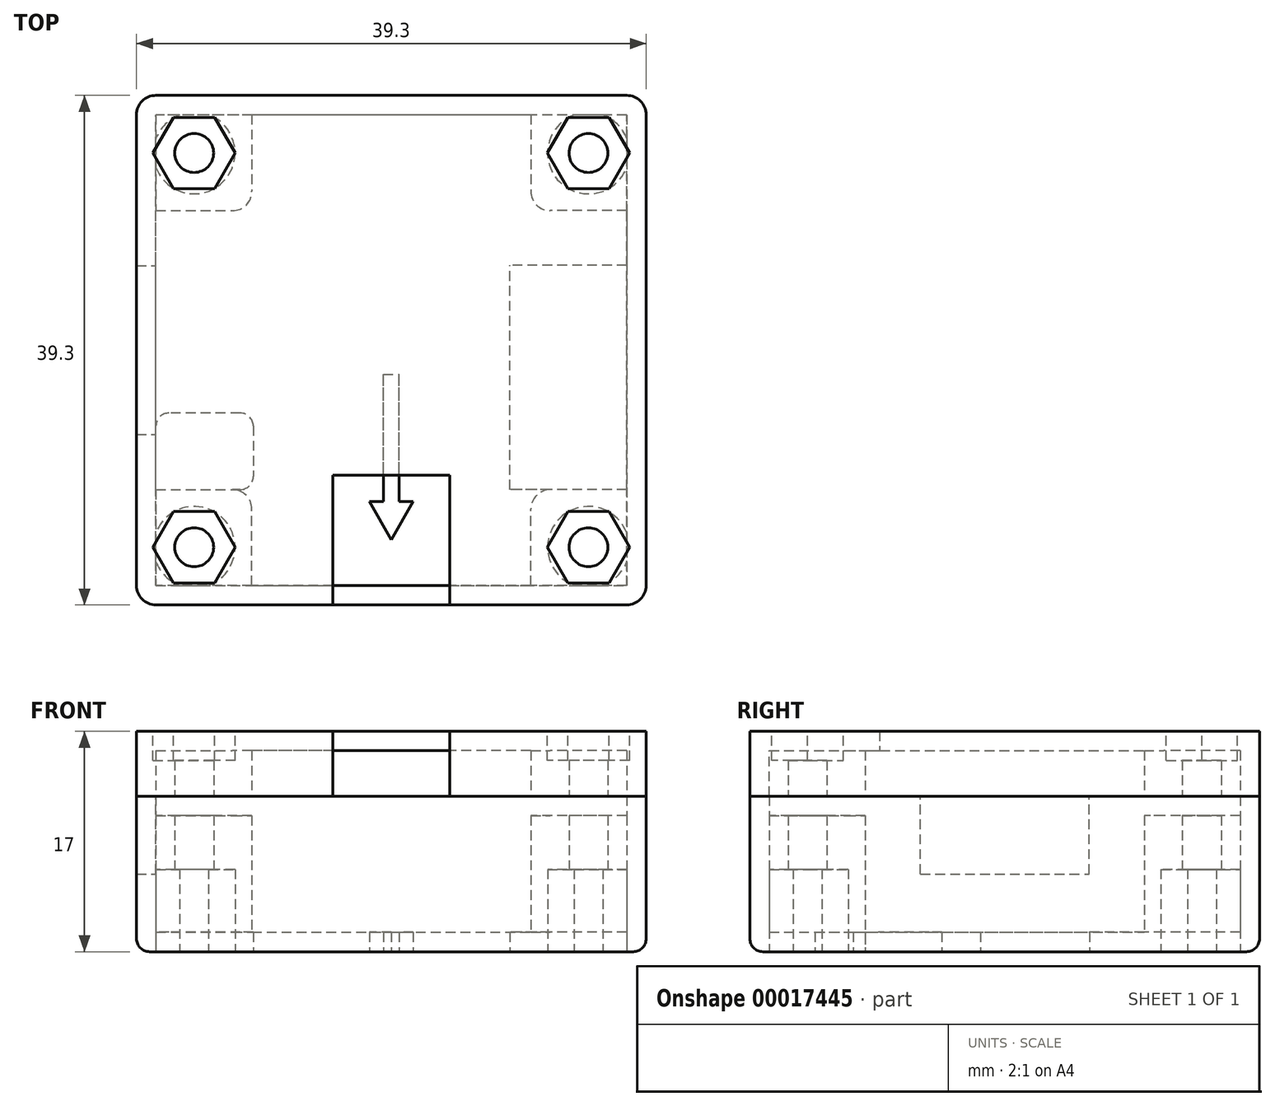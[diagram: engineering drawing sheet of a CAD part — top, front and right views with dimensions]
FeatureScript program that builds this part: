
annotation { "Feature Type Name" : "Feature", "Feature Type Description" : "" }
export const myFeature = defineFeature(function(context is Context, id is Id, definition is map)
    precondition{}
    {
        {
            var Q0;
            Q0=qCreatedBy(makeId("Top.planeOp"),FACE);
            var sketch = newSketch(context, id + "F0", { "sketchPlane" : qUnion([Q0])});
            skLineSegment(sketch, "E0.rect.bottom", {"start": v(18.15, -19.65) * mm, "end": v(-18.15, -19.65) * mm});
            skLineSegment(sketch, "E0.rect.top", {"start": v(18.15, 19.65) * mm, "end": v(-18.15, 19.65) * mm});
            skLineSegment(sketch, "E0.rect.left", {"start": v(19.65, -18.15) * mm, "end": v(19.65, 18.15) * mm});
            skLineSegment(sketch, "E0.rect.right", {"start": v(-19.65, -18.15) * mm, "end": v(-19.65, 18.15) * mm});
            skPoint(sketch, "E0.rect.middle", {"position": v(0, 0) * mm});
            skCircle(sketch, "E1", {"center": v(0, 0) * mm, "radius": 21.5 * mm, "construction": true});
            skLineSegment(sketch, "E2", {"start": v(0, 0) * mm, "end": v(19.65, 19.65) * mm, "construction": true});
            skCircle(sketch, "E3", {"center": v(15.2, 15.2) * mm, "radius": 1.5 * mm});
            skArc(sketch, "E4", {"start": v(14.1, 18.15) * mm, "mid": v(12.98, 12.98) * mm, "end": v(18.15, 14.1) * mm});
            skPoint(sketch, "E5.visualSharp", {"position": v(19.65, 19.65) * mm});
            skArc(sketch, "E5.filletArc", {"start": v(19.65, 18.15) * mm, "mid": v(19.21, 19.21) * mm, "end": v(18.15, 19.65) * mm});
            skLineSegment(sketch, "E6.rect.bottom", {"start": v(18.15, 19.65) * mm, "end": v(10.76, 19.65) * mm});
            skLineSegment(sketch, "E6.rect.top", {"start": v(18.15, 10.76) * mm, "end": v(12.26, 10.76) * mm});
            skLineSegment(sketch, "E6.rect.left", {"start": v(19.65, 18.15) * mm, "end": v(19.65, 10.76) * mm});
            skLineSegment(sketch, "E6.rect.right", {"start": v(10.76, 18.15) * mm, "end": v(10.76, 12.26) * mm});
            skPoint(sketch, "E7.visualSharp", {"position": v(10.76, 10.76) * mm});
            skArc(sketch, "E7.filletArc", {"start": v(10.76, 12.26) * mm, "mid": v(11.2, 11.2) * mm, "end": v(12.26, 10.76) * mm});
            skArc(sketch, "E8.1.1", {"start": v(-16.31, 18.15) * mm, "mid": v(-17.43, 17.43) * mm, "end": v(-18.15, 16.31) * mm});
            skCircle(sketch, "E8.1.2", {"center": v(-15.2, 15.2) * mm, "radius": 1.5 * mm});
            skLineSegment(sketch, "E8.1.3", {"start": v(-18.15, 10.76) * mm, "end": v(-12.26, 10.76) * mm});
            skArc(sketch, "E8.1.4", {"start": v(-12.26, 10.76) * mm, "mid": v(-11.2, 11.2) * mm, "end": v(-10.76, 12.26) * mm});
            skLineSegment(sketch, "E8.1.5", {"start": v(-10.76, 18.15) * mm, "end": v(-10.76, 12.26) * mm});
            skLineSegment(sketch, "E8.1.6", {"start": v(-18.15, 19.65) * mm, "end": v(-10.76, 19.65) * mm});
            skArc(sketch, "E8.1.7", {"start": v(-18.15, 19.65) * mm, "mid": v(-19.21, 19.21) * mm, "end": v(-19.65, 18.15) * mm});
            skLineSegment(sketch, "E8.1.8", {"start": v(-19.65, 18.15) * mm, "end": v(-19.65, 10.76) * mm});
            skArc(sketch, "E8.2.1", {"start": v(-18.15, -16.31) * mm, "mid": v(-17.43, -17.43) * mm, "end": v(-16.31, -18.15) * mm});
            skCircle(sketch, "E8.2.2", {"center": v(-15.2, -15.2) * mm, "radius": 1.5 * mm});
            skLineSegment(sketch, "E8.2.3", {"start": v(-10.76, -18.15) * mm, "end": v(-10.76, -12.26) * mm});
            skArc(sketch, "E8.2.4", {"start": v(-10.76, -12.26) * mm, "mid": v(-11.2, -11.2) * mm, "end": v(-12.26, -10.76) * mm});
            skLineSegment(sketch, "E8.2.5", {"start": v(-18.15, -10.76) * mm, "end": v(-12.26, -10.76) * mm});
            skLineSegment(sketch, "E8.2.6", {"start": v(-19.65, -18.15) * mm, "end": v(-19.65, -10.76) * mm});
            skArc(sketch, "E8.2.7", {"start": v(-19.65, -18.15) * mm, "mid": v(-19.21, -19.21) * mm, "end": v(-18.15, -19.65) * mm});
            skLineSegment(sketch, "E8.2.8", {"start": v(-18.15, -19.65) * mm, "end": v(-10.76, -19.65) * mm});
            skArc(sketch, "E9.2.3.0", {"start": v(18.15, -14.1) * mm, "mid": v(12.98, -12.98) * mm, "end": v(14.1, -18.15) * mm});
            skCircle(sketch, "E9.4.3.0", {"center": v(15.2, -15.2) * mm, "radius": 1.5 * mm});
            skArc(sketch, "E9.9.3.0", {"start": v(12.26, -10.76) * mm, "mid": v(11.2, -11.2) * mm, "end": v(10.76, -12.26) * mm});
            skLineSegment(sketch, "E9.16.3.0", {"start": v(18.15, -19.65) * mm, "end": v(10.76, -19.65) * mm});
            skArc(sketch, "E9.19.3.0", {"start": v(18.15, -19.65) * mm, "mid": v(19.21, -19.21) * mm, "end": v(19.65, -18.15) * mm});
            skLineSegment(sketch, "E9.23.3.0", {"start": v(19.65, -18.15) * mm, "end": v(19.65, -10.76) * mm});
            skPoint(sketch, "E10.orphan", {"position": v(-19.65, 19.65) * mm});
            skPoint(sketch, "E11.orphan", {"position": v(19.65, -19.65) * mm});
            skPoint(sketch, "E12.orphan", {"position": v(-19.65, -19.65) * mm});
            skLineSegment(sketch, "E13.trimOffspring", {"start": v(14.1, 18.15) * mm, "end": v(-14.1, 18.15) * mm});
            skLineSegment(sketch, "E14.trimOffspring", {"start": v(-18.15, -14.1) * mm, "end": v(-18.15, 14.1) * mm});
            skLineSegment(sketch, "E15.trimOffspring", {"start": v(14.1, -18.15) * mm, "end": v(-14.1, -18.15) * mm});
            skLineSegment(sketch, "E16.trimOffspring", {"start": v(18.15, -14.1) * mm, "end": v(18.15, 14.1) * mm});
            skLineSegment(sketch, "E17", {"start": v(-14.1, 18.15) * mm, "end": v(-18.15, 18.15) * mm});
            skLineSegment(sketch, "E18", {"start": v(-18.15, 18.15) * mm, "end": v(-18.15, 14.1) * mm});
            skLineSegment(sketch, "E19", {"start": v(14.1, 18.15) * mm, "end": v(18.15, 18.15) * mm});
            skLineSegment(sketch, "E20", {"start": v(18.15, 18.15) * mm, "end": v(18.15, 14.1) * mm});
            skLineSegment(sketch, "E21", {"start": v(18.15, -14.1) * mm, "end": v(18.15, -18.15) * mm});
            skLineSegment(sketch, "E22", {"start": v(14.1, -18.15) * mm, "end": v(18.15, -18.15) * mm});
            skLineSegment(sketch, "E23", {"start": v(-14.1, -18.15) * mm, "end": v(-18.15, -18.15) * mm});
            skLineSegment(sketch, "E24", {"start": v(-18.15, -14.1) * mm, "end": v(-18.15, -18.15) * mm});
            skLineSegment(sketch, "E25.trimOffspring", {"start": v(18.15, -10.76) * mm, "end": v(12.26, -10.76) * mm});
            skLineSegment(sketch, "E26.trimOffspring", {"start": v(10.76, -18.15) * mm, "end": v(10.76, -12.26) * mm});
            skArc(sketch, "E27.trimOffspring", {"start": v(-18.15, 14.1) * mm, "mid": v(-12.98, 12.98) * mm, "end": v(-14.1, 18.15) * mm});
            skArc(sketch, "E28.trimOffspring", {"start": v(18.15, 16.31) * mm, "mid": v(17.43, 17.43) * mm, "end": v(16.31, 18.15) * mm});
            skArc(sketch, "E29.trimOffspring", {"start": v(16.31, -18.15) * mm, "mid": v(17.43, -17.43) * mm, "end": v(18.15, -16.31) * mm});
            skArc(sketch, "E30.trimOffspring", {"start": v(-14.1, -18.15) * mm, "mid": v(-12.98, -12.98) * mm, "end": v(-18.15, -14.1) * mm});
            skLineSegment(sketch, "E31", {"start": v(-26.46, -4.85) * mm, "end": v(25.33, -4.85) * mm, "construction": true});
            skLineSegment(sketch, "E32", {"start": v(-10.65, -23.17) * mm, "end": v(-10.65, 21.13) * mm, "construction": true});
            skLineSegment(sketch, "E33.bottom", {"start": v(-11.65, -4.85) * mm, "end": v(-17.15, -4.85) * mm});
            skLineSegment(sketch, "E33.top", {"start": v(-11.65, -10.76) * mm, "end": v(-17.15, -10.76) * mm});
            skLineSegment(sketch, "E33.left", {"start": v(-10.65, -5.85) * mm, "end": v(-10.65, -9.76) * mm});
            skLineSegment(sketch, "E33.right", {"start": v(-18.15, -5.85) * mm, "end": v(-18.15, -9.76) * mm});
            skPoint(sketch, "E34.visualSharp", {"position": v(-10.65, -10.76) * mm});
            skArc(sketch, "E34.filletArc", {"start": v(-11.65, -10.76) * mm, "mid": v(-10.94, -10.46) * mm, "end": v(-10.65, -9.76) * mm});
            skPoint(sketch, "E35.visualSharp", {"position": v(-10.65, -4.85) * mm});
            skArc(sketch, "E35.filletArc", {"start": v(-10.65, -5.85) * mm, "mid": v(-10.94, -5.14) * mm, "end": v(-11.65, -4.85) * mm});
            skPoint(sketch, "E36.visualSharp", {"position": v(-18.15, -4.85) * mm});
            skArc(sketch, "E36.filletArc", {"start": v(-17.15, -4.85) * mm, "mid": v(-17.86, -5.14) * mm, "end": v(-18.15, -5.85) * mm});
            skPoint(sketch, "E37.visualSharp", {"position": v(-18.15, -10.76) * mm});
            skArc(sketch, "E37.filletArc", {"start": v(-18.15, -9.76) * mm, "mid": v(-17.86, -10.46) * mm, "end": v(-17.15, -10.76) * mm});
            skLineSegment(sketch, "E38", {"start": v(9.15, -24.31) * mm, "end": v(9.15, 23.94) * mm, "construction": true});
            skLineSegment(sketch, "E39", {"start": v(-23.3, 6.55) * mm, "end": v(24.8, 6.55) * mm, "construction": true});
            skLineSegment(sketch, "E40.bottom", {"start": v(18.15, -10.76) * mm, "end": v(9.15, -10.76) * mm});
            skLineSegment(sketch, "E40.top", {"start": v(18.15, 6.55) * mm, "end": v(9.15, 6.55) * mm});
            skLineSegment(sketch, "E40.left", {"start": v(18.15, -10.76) * mm, "end": v(18.15, 6.55) * mm});
            skLineSegment(sketch, "E40.right", {"start": v(9.15, -10.76) * mm, "end": v(9.15, 6.55) * mm});
            skLineSegment(sketch, "E41", {"start": v(0, -14.62) * mm, "end": v(1.68, -11.69) * mm});
            skLineSegment(sketch, "E42", {"start": v(1.68, -11.69) * mm, "end": v(0.61, -11.69) * mm});
            skLineSegment(sketch, "E43", {"start": v(0.61, -11.69) * mm, "end": v(0.61, -1.87) * mm});
            skLineSegment(sketch, "E44", {"start": v(0.61, -1.87) * mm, "end": v(0, -1.87) * mm});
            skLineSegment(sketch, "E45.MirrorCS", {"start": v(0, -14.62) * mm, "end": v(-1.68, -11.69) * mm});
            skLineSegment(sketch, "E46.MirrorCS", {"start": v(-1.68, -11.69) * mm, "end": v(-0.61, -11.69) * mm});
            skLineSegment(sketch, "E47.MirrorCS", {"start": v(-0.61, -11.69) * mm, "end": v(-0.61, -1.87) * mm});
            skLineSegment(sketch, "E48.MirrorCS", {"start": v(-0.61, -1.87) * mm, "end": v(0, -1.87) * mm});
            skSolve(sketch);
        }
        {
            var Q0;
            Q0=makeQuery(id+"F0.imprint","IMPRINT",FACE,{"disambiguationData":[TD([[makeQuery(id+"F0.imprint","IMPRINT",EDGE,{"derivedFrom":sQuery(id+"F0.wireOp",EDGE,"E0.rect.bottom")}),-1.0]])]});
            extrude(context, id + "F1", {"entities" : qUnion([Q0]), "depth" : 12 * mm});
        }
        {
            var Q0;
            {var subQ2=sQuery(id+"F0.wireOp",EDGE,"E8.1.3");Q0=makeQuery(id+"F0.imprint","IMPRINT",FACE,{"disambiguationData":[TD([[makeQuery(id+"F0.imprint","IMPRINT",EDGE,{"derivedFrom":subQ2}),1.0]])]});}
            var Q1;
            {var subQ3=sQuery(id+"F0.wireOp",EDGE,"E8.1.1");Q1=makeQuery(id+"F0.imprint","IMPRINT",FACE,{"disambiguationData":[TD([[makeQuery(id+"F0.imprint","IMPRINT",EDGE,{"derivedFrom":subQ3}),-1.0]])]});}
            var Q2;
            {var subQ2=sQuery(id+"F0.wireOp",EDGE,"E4");Q2=makeQuery(id+"F0.imprint","IMPRINT",FACE,{"disambiguationData":[TD([[makeQuery(id+"F0.imprint","IMPRINT",EDGE,{"derivedFrom":subQ2}),-1.0]])]});}
            var Q3;
            {var subQ0=sQuery(id+"F0.wireOp",EDGE,"E28.trimOffspring");Q3=makeQuery(id+"F0.imprint","IMPRINT",FACE,{"disambiguationData":[TD([[makeQuery(id+"F0.imprint","IMPRINT",EDGE,{"derivedFrom":subQ0}),-1.0]])]});}
            var Q4;
            {var subQ2=sQuery(id+"F0.wireOp",EDGE,"E8.2.3");Q4=makeQuery(id+"F0.imprint","IMPRINT",FACE,{"disambiguationData":[TD([[makeQuery(id+"F0.imprint","IMPRINT",EDGE,{"derivedFrom":subQ2}),1.0]])]});}
            var Q5;
            {var subQ3=sQuery(id+"F0.wireOp",EDGE,"E8.2.1");Q5=makeQuery(id+"F0.imprint","IMPRINT",FACE,{"disambiguationData":[TD([[makeQuery(id+"F0.imprint","IMPRINT",EDGE,{"derivedFrom":subQ3}),-1.0]])]});}
            var Q6;
            {var subQ3=sQuery(id+"F0.wireOp",EDGE,"E9.2.3.0");Q6=makeQuery(id+"F0.imprint","IMPRINT",FACE,{"disambiguationData":[TD([[makeQuery(id+"F0.imprint","IMPRINT",EDGE,{"derivedFrom":subQ3}),-1.0]])]});}
            var Q7;
            {var subQ0=sQuery(id+"F0.wireOp",EDGE,"E29.trimOffspring");Q7=makeQuery(id+"F0.imprint","IMPRINT",FACE,{"disambiguationData":[TD([[makeQuery(id+"F0.imprint","IMPRINT",EDGE,{"derivedFrom":subQ0}),-1.0]])]});}
            extrude(context, id + "F2", {"entities" : qUnion([Q0, Q1, Q2, Q3, Q4, Q5, Q6, Q7]), "operationType" : NewBodyOperationType.ADD, "depth" : 10.5 * mm});
        }
        {
            var Q0;
            {var subQ2=sQuery(id+"F0.wireOp",EDGE,"E8.1.1");Q0=makeQuery(id+"F0.imprint","IMPRINT",FACE,{"disambiguationData":[TD([[makeQuery(id+"F0.imprint","IMPRINT",EDGE,{"derivedFrom":subQ2}),1.0]])]});}
            var Q1;
            Q1=makeQuery(id+"F0.imprint","IMPRINT",FACE,{"disambiguationData":[TD([[makeQuery(id+"F0.imprint","IMPRINT",EDGE,{"derivedFrom":sQuery(id+"F0.wireOp",EDGE,"E3")}),-1.0]])]});
            var Q2;
            {var subQ2=sQuery(id+"F0.wireOp",EDGE,"E9.2.3.0");Q2=makeQuery(id+"F0.imprint","IMPRINT",FACE,{"disambiguationData":[TD([[makeQuery(id+"F0.imprint","IMPRINT",EDGE,{"derivedFrom":subQ2}),1.0]])]});}
            var Q3;
            {var subQ2=sQuery(id+"F0.wireOp",EDGE,"E8.2.1");Q3=makeQuery(id+"F0.imprint","IMPRINT",FACE,{"disambiguationData":[TD([[makeQuery(id+"F0.imprint","IMPRINT",EDGE,{"derivedFrom":subQ2}),1.0]])]});}
            extrude(context, id + "F3", {"entities" : qUnion([Q0, Q1, Q2, Q3]), "operationType" : NewBodyOperationType.ADD, "depth" : 10.5 * mm, "hasSecondDirection" : true, "secondDirectionOppositeDirection" : false, "secondDirectionDepth" : 6.35 * mm});
        }
        {
            var Q0;
            Q0 = qSketchRegion(id + "F0", true);
            var Q1;
            {var subQ2=sQuery(id+"F0.wireOp",EDGE,"E6.rect.top");Q1=makeQuery(id+"F0.imprint","IMPRINT",FACE,{"disambiguationData":[TD([[makeQuery(id+"F0.imprint","IMPRINT",EDGE,{"derivedFrom":subQ2}),1.0]])]});}
            extrude(context, id + "F4", {"entities" : qUnion([Q0, Q1]), "operationType" : NewBodyOperationType.ADD, "depth" : 1.5 * mm});
        }
        {
            var Q0;
            Q0=makeQuery(id+"F0.imprint","IMPRINT",FACE,{"disambiguationData":[TD([[makeQuery(id+"F0.imprint","IMPRINT",EDGE,{"derivedFrom":sQuery(id+"F0.wireOp",EDGE,"E33.bottom")}),1.0]])]});
            extrude(context, id + "F5", {"entities" : qUnion([Q0]), "operationType" : NewBodyOperationType.REMOVE, "depth" : 1.5 * mm});
        }
        {
            var Q0;
            Q0=makeQuery(id+"F0.imprint","IMPRINT",FACE,{"disambiguationData":[TD([[makeQuery(id+"F0.imprint","IMPRINT",EDGE,{"derivedFrom":sQuery(id+"F0.wireOp",EDGE,"E40.top")}),1.0]])]});
            extrude(context, id + "F6", {"entities" : qUnion([Q0]), "operationType" : NewBodyOperationType.REMOVE, "depth" : 1.5 * mm});
        }
        {
            var Q0;
            Q0=makeQuery(id+"F0.imprint","IMPRINT",FACE,{"disambiguationData":[TD([[makeQuery(id+"F0.imprint","IMPRINT",EDGE,{"derivedFrom":sQuery(id+"F0.wireOp",EDGE,"E41")}),1.0]])]});
            extrude(context, id + "F7", {"entities" : qUnion([Q0]), "operationType" : NewBodyOperationType.REMOVE, "depth" : 1.5 * mm});
        }
        {
            var Q0;
            Q0=makeQuery(id+"F1.opExtrude","CAP_FACE",FACE,{"disambiguationData":[OSD([sQuery(id+"F0.wireOp",EDGE,"E0.rect.bottom"),sQuery(id+"F0.wireOp",EDGE,"E0.rect.top"),sQuery(id+"F0.wireOp",EDGE,"E0.rect.left"),sQuery(id+"F0.wireOp",EDGE,"E0.rect.right"),sQuery(id+"F0.wireOp",EDGE,"E5.filletArc"),sQuery(id+"F0.wireOp",EDGE,"E6.rect.bottom"),sQuery(id+"F0.wireOp",EDGE,"E6.rect.left"),sQuery(id+"F0.wireOp",EDGE,"E8.1.6"),sQuery(id+"F0.wireOp",EDGE,"E8.1.7"),sQuery(id+"F0.wireOp",EDGE,"E8.1.8"),sQuery(id+"F0.wireOp",EDGE,"E8.2.6"),sQuery(id+"F0.wireOp",EDGE,"E8.2.7"),sQuery(id+"F0.wireOp",EDGE,"E8.2.8"),sQuery(id+"F0.wireOp",EDGE,"E9.16.3.0"),sQuery(id+"F0.wireOp",EDGE,"E9.19.3.0"),sQuery(id+"F0.wireOp",EDGE,"E9.23.3.0"),sQuery(id+"F0.wireOp",EDGE,"E13.trimOffspring"),sQuery(id+"F0.wireOp",EDGE,"E14.trimOffspring"),sQuery(id+"F0.wireOp",EDGE,"E15.trimOffspring"),sQuery(id+"F0.wireOp",EDGE,"E16.trimOffspring"),sQuery(id+"F0.wireOp",EDGE,"E17"),sQuery(id+"F0.wireOp",EDGE,"E18"),sQuery(id+"F0.wireOp",EDGE,"E19"),sQuery(id+"F0.wireOp",EDGE,"E20"),sQuery(id+"F0.wireOp",EDGE,"E21"),sQuery(id+"F0.wireOp",EDGE,"E22"),sQuery(id+"F0.wireOp",EDGE,"E23"),sQuery(id+"F0.wireOp",EDGE,"E24"),sQuery(id+"F0.wireOp",EDGE,"E33.right"),sQuery(id+"F0.wireOp",EDGE,"E40.left")])],"isStart":false});
            var sketch = newSketch(context, id + "F8", { "sketchPlane" : qUnion([Q0])});
            skLineSegment(sketch, "E49.bottom", {"start": v(-19.65, 6.5) * mm, "end": v(-18.15, 6.5) * mm});
            skLineSegment(sketch, "E49.top", {"start": v(-19.65, -6.5) * mm, "end": v(-18.15, -6.5) * mm});
            skLineSegment(sketch, "E49.left", {"start": v(-19.65, 6.5) * mm, "end": v(-19.65, -6.5) * mm});
            skLineSegment(sketch, "E49.right", {"start": v(-18.15, 6.5) * mm, "end": v(-18.15, -6.5) * mm});
            skLineSegment(sketch, "E50", {"start": v(-25.19, 6.5) * mm, "end": v(-14.9, 6.5) * mm, "construction": true});
            skSolve(sketch);
        }
        {
            var Q0;
            Q0 = qSketchRegion(id + "F8", true);
            extrude(context, id + "F9", {"entities" : qUnion([Q0]), "operationType" : NewBodyOperationType.REMOVE, "oppositeDirection" : true, "depth" : 6 * mm});
        }
        {
            var Q0;
            Q0=makeQuery(id+"F1.opExtrude","CAP_EDGE",EDGE,{"disambiguationData":[OSD([sQuery(id+"F0.wireOp",EDGE,"E0.rect.left"),sQuery(id+"F0.wireOp",EDGE,"E6.rect.left"),sQuery(id+"F0.wireOp",EDGE,"E9.23.3.0")])],"isStart":true});
            fillet(context, id + "F10", {"entities" : qUnion([Q0]), "radius" : 1 * mm, "tangentPropagation" : true, "allowEdgeOverflow" : false});
        }
        {
            var Q0;
            Q0=makeQuery(id+"F1.opExtrude","CAP_FACE",FACE,{"disambiguationData":[OSD([sQuery(id+"F0.wireOp",EDGE,"E0.rect.bottom"),sQuery(id+"F0.wireOp",EDGE,"E0.rect.top"),sQuery(id+"F0.wireOp",EDGE,"E0.rect.left"),sQuery(id+"F0.wireOp",EDGE,"E0.rect.right"),sQuery(id+"F0.wireOp",EDGE,"E5.filletArc"),sQuery(id+"F0.wireOp",EDGE,"E6.rect.bottom"),sQuery(id+"F0.wireOp",EDGE,"E6.rect.left"),sQuery(id+"F0.wireOp",EDGE,"E8.1.6"),sQuery(id+"F0.wireOp",EDGE,"E8.1.7"),sQuery(id+"F0.wireOp",EDGE,"E8.1.8"),sQuery(id+"F0.wireOp",EDGE,"E8.2.6"),sQuery(id+"F0.wireOp",EDGE,"E8.2.7"),sQuery(id+"F0.wireOp",EDGE,"E8.2.8"),sQuery(id+"F0.wireOp",EDGE,"E9.16.3.0"),sQuery(id+"F0.wireOp",EDGE,"E9.19.3.0"),sQuery(id+"F0.wireOp",EDGE,"E9.23.3.0"),sQuery(id+"F0.wireOp",EDGE,"E13.trimOffspring"),sQuery(id+"F0.wireOp",EDGE,"E14.trimOffspring"),sQuery(id+"F0.wireOp",EDGE,"E15.trimOffspring"),sQuery(id+"F0.wireOp",EDGE,"E16.trimOffspring"),sQuery(id+"F0.wireOp",EDGE,"E17"),sQuery(id+"F0.wireOp",EDGE,"E18"),sQuery(id+"F0.wireOp",EDGE,"E19"),sQuery(id+"F0.wireOp",EDGE,"E20"),sQuery(id+"F0.wireOp",EDGE,"E21"),sQuery(id+"F0.wireOp",EDGE,"E22"),sQuery(id+"F0.wireOp",EDGE,"E23"),sQuery(id+"F0.wireOp",EDGE,"E24"),sQuery(id+"F0.wireOp",EDGE,"E33.right"),sQuery(id+"F0.wireOp",EDGE,"E40.left")])],"isStart":false});
            cPlane(context, id + "F11", {"entities" : qUnion([Q0]), "cplaneType" : CPlaneType.OFFSET, "offset" : 0 * mm, "width" : 150 * mm, "height" : 150 * mm});
        }
        {
            var Q0;
            Q0=qCreatedBy(id+"F11.planeOp",FACE);
            var sketch = newSketch(context, id + "F12", { "sketchPlane" : qUnion([Q0])});
            skLineSegment(sketch, "E51.rect.bottom", {"start": v(18.15, -19.65) * mm, "end": v(-18.15, -19.65) * mm});
            skLineSegment(sketch, "E51.rect.top", {"start": v(18.15, 19.65) * mm, "end": v(-18.15, 19.65) * mm});
            skLineSegment(sketch, "E51.rect.left", {"start": v(19.65, -18.15) * mm, "end": v(19.65, 18.15) * mm});
            skLineSegment(sketch, "E51.rect.right", {"start": v(-19.65, -18.15) * mm, "end": v(-19.65, 18.15) * mm});
            skPoint(sketch, "E51.rect.middle", {"position": v(0, 0) * mm});
            skCircle(sketch, "E52", {"center": v(0, 0) * mm, "radius": 21.5 * mm, "construction": true});
            skLineSegment(sketch, "E53", {"start": v(0, 0) * mm, "end": v(19.65, 19.65) * mm, "construction": true});
            skCircle(sketch, "E54", {"center": v(15.2, 15.2) * mm, "radius": 1.5 * mm});
            skArc(sketch, "E55", {"start": v(14.1, 18.15) * mm, "mid": v(12.98, 12.98) * mm, "end": v(18.15, 14.1) * mm});
            skPoint(sketch, "E56.visualSharp", {"position": v(19.65, 19.65) * mm});
            skArc(sketch, "E56.filletArc", {"start": v(19.65, 18.15) * mm, "mid": v(19.21, 19.21) * mm, "end": v(18.15, 19.65) * mm});
            skLineSegment(sketch, "E57.rect.bottom", {"start": v(18.15, 19.65) * mm, "end": v(10.76, 19.65) * mm});
            skLineSegment(sketch, "E57.rect.top", {"start": v(18.15, 10.76) * mm, "end": v(12.26, 10.76) * mm});
            skLineSegment(sketch, "E57.rect.left", {"start": v(19.65, 18.15) * mm, "end": v(19.65, 10.76) * mm});
            skLineSegment(sketch, "E57.rect.right", {"start": v(10.76, 18.15) * mm, "end": v(10.76, 12.26) * mm});
            skPoint(sketch, "E58.visualSharp", {"position": v(10.76, 10.76) * mm});
            skArc(sketch, "E58.filletArc", {"start": v(10.76, 12.26) * mm, "mid": v(11.2, 11.2) * mm, "end": v(12.26, 10.76) * mm});
            skArc(sketch, "E59.1.1", {"start": v(-16.31, 18.15) * mm, "mid": v(-17.43, 17.43) * mm, "end": v(-18.15, 16.31) * mm});
            skCircle(sketch, "E59.1.2", {"center": v(-15.2, 15.2) * mm, "radius": 1.5 * mm});
            skLineSegment(sketch, "E59.1.3", {"start": v(-18.15, 10.76) * mm, "end": v(-12.26, 10.76) * mm});
            skArc(sketch, "E59.1.4", {"start": v(-12.26, 10.76) * mm, "mid": v(-11.2, 11.2) * mm, "end": v(-10.76, 12.26) * mm});
            skLineSegment(sketch, "E59.1.5", {"start": v(-10.76, 18.15) * mm, "end": v(-10.76, 12.26) * mm});
            skLineSegment(sketch, "E59.1.6", {"start": v(-18.15, 19.65) * mm, "end": v(-10.76, 19.65) * mm});
            skArc(sketch, "E59.1.7", {"start": v(-18.15, 19.65) * mm, "mid": v(-19.21, 19.21) * mm, "end": v(-19.65, 18.15) * mm});
            skLineSegment(sketch, "E59.1.8", {"start": v(-19.65, 18.15) * mm, "end": v(-19.65, 10.76) * mm});
            skArc(sketch, "E59.2.1", {"start": v(-18.15, -16.31) * mm, "mid": v(-17.43, -17.43) * mm, "end": v(-16.31, -18.15) * mm});
            skCircle(sketch, "E59.2.2", {"center": v(-15.2, -15.2) * mm, "radius": 1.5 * mm});
            skLineSegment(sketch, "E59.2.3", {"start": v(-10.76, -18.15) * mm, "end": v(-10.76, -12.26) * mm});
            skArc(sketch, "E59.2.4", {"start": v(-10.76, -12.26) * mm, "mid": v(-11.2, -11.2) * mm, "end": v(-12.26, -10.76) * mm});
            skLineSegment(sketch, "E59.2.5", {"start": v(-18.15, -10.76) * mm, "end": v(-12.26, -10.76) * mm});
            skLineSegment(sketch, "E59.2.6", {"start": v(-19.65, -18.15) * mm, "end": v(-19.65, -10.76) * mm});
            skArc(sketch, "E59.2.7", {"start": v(-19.65, -18.15) * mm, "mid": v(-19.21, -19.21) * mm, "end": v(-18.15, -19.65) * mm});
            skLineSegment(sketch, "E59.2.8", {"start": v(-18.15, -19.65) * mm, "end": v(-10.76, -19.65) * mm});
            skArc(sketch, "E60.2.3.0", {"start": v(18.15, -14.1) * mm, "mid": v(12.98, -12.98) * mm, "end": v(14.1, -18.15) * mm});
            skCircle(sketch, "E60.4.3.0", {"center": v(15.2, -15.2) * mm, "radius": 1.5 * mm});
            skArc(sketch, "E60.9.3.0", {"start": v(12.26, -10.76) * mm, "mid": v(11.2, -11.2) * mm, "end": v(10.76, -12.26) * mm});
            skLineSegment(sketch, "E60.16.3.0", {"start": v(18.15, -19.65) * mm, "end": v(10.76, -19.65) * mm});
            skArc(sketch, "E60.19.3.0", {"start": v(18.15, -19.65) * mm, "mid": v(19.21, -19.21) * mm, "end": v(19.65, -18.15) * mm});
            skLineSegment(sketch, "E60.23.3.0", {"start": v(19.65, -18.15) * mm, "end": v(19.65, -10.76) * mm});
            skPoint(sketch, "E61.orphan", {"position": v(-19.65, 19.65) * mm});
            skPoint(sketch, "E62.orphan", {"position": v(19.65, -19.65) * mm});
            skPoint(sketch, "E63.orphan", {"position": v(-19.65, -19.65) * mm});
            skLineSegment(sketch, "E64.trimOffspring", {"start": v(14.1, 18.15) * mm, "end": v(-14.1, 18.15) * mm});
            skLineSegment(sketch, "E65.trimOffspring", {"start": v(-18.15, -14.1) * mm, "end": v(-18.15, 14.1) * mm});
            skLineSegment(sketch, "E66.trimOffspring", {"start": v(14.1, -18.15) * mm, "end": v(-14.1, -18.15) * mm});
            skLineSegment(sketch, "E67.trimOffspring", {"start": v(18.15, -14.1) * mm, "end": v(18.15, 14.1) * mm});
            skLineSegment(sketch, "E68", {"start": v(-14.1, 18.15) * mm, "end": v(-18.15, 18.15) * mm});
            skLineSegment(sketch, "E69", {"start": v(-18.15, 18.15) * mm, "end": v(-18.15, 14.1) * mm});
            skLineSegment(sketch, "E70", {"start": v(14.1, 18.15) * mm, "end": v(18.15, 18.15) * mm});
            skLineSegment(sketch, "E71", {"start": v(18.15, 18.15) * mm, "end": v(18.15, 14.1) * mm});
            skLineSegment(sketch, "E72", {"start": v(18.15, -14.1) * mm, "end": v(18.15, -18.15) * mm});
            skLineSegment(sketch, "E73", {"start": v(14.1, -18.15) * mm, "end": v(18.15, -18.15) * mm});
            skLineSegment(sketch, "E74", {"start": v(-14.1, -18.15) * mm, "end": v(-18.15, -18.15) * mm});
            skLineSegment(sketch, "E75", {"start": v(-18.15, -14.1) * mm, "end": v(-18.15, -18.15) * mm});
            skLineSegment(sketch, "E76.trimOffspring", {"start": v(18.15, -10.76) * mm, "end": v(12.26, -10.76) * mm});
            skLineSegment(sketch, "E77.trimOffspring", {"start": v(10.76, -18.15) * mm, "end": v(10.76, -12.26) * mm});
            skArc(sketch, "E78.trimOffspring", {"start": v(-18.15, 14.1) * mm, "mid": v(-12.98, 12.98) * mm, "end": v(-14.1, 18.15) * mm});
            skArc(sketch, "E79.trimOffspring", {"start": v(18.15, 16.31) * mm, "mid": v(17.43, 17.43) * mm, "end": v(16.31, 18.15) * mm});
            skArc(sketch, "E80.trimOffspring", {"start": v(16.31, -18.15) * mm, "mid": v(17.43, -17.43) * mm, "end": v(18.15, -16.31) * mm});
            skArc(sketch, "E81.trimOffspring", {"start": v(-14.1, -18.15) * mm, "mid": v(-12.98, -12.98) * mm, "end": v(-18.15, -14.1) * mm});
            skLineSegment(sketch, "E82", {"start": v(-26.46, -4.85) * mm, "end": v(25.33, -4.85) * mm, "construction": true});
            skLineSegment(sketch, "E83", {"start": v(-10.65, -23.17) * mm, "end": v(-10.65, 21.13) * mm, "construction": true});
            skLineSegment(sketch, "E84.right", {"start": v(-18.15, -5.85) * mm, "end": v(-18.15, -9.76) * mm});
            skPoint(sketch, "E85.visualSharp", {"position": v(-10.65, -10.76) * mm});
            skPoint(sketch, "E86.visualSharp", {"position": v(-10.65, -4.85) * mm});
            skPoint(sketch, "E87.visualSharp", {"position": v(-18.15, -4.85) * mm});
            skPoint(sketch, "E88.visualSharp", {"position": v(-18.15, -10.76) * mm});
            skLineSegment(sketch, "E89", {"start": v(9.15, -24.31) * mm, "end": v(9.15, 23.94) * mm, "construction": true});
            skLineSegment(sketch, "E90", {"start": v(-23.3, 6.55) * mm, "end": v(24.8, 6.55) * mm, "construction": true});
            skLineSegment(sketch, "E91.left", {"start": v(18.15, -10.76) * mm, "end": v(18.15, 6.55) * mm});
            skSolve(sketch);
        }
        {
            var Q0;
            Q0=makeQuery(id+"F12.imprint","IMPRINT",FACE,{"disambiguationData":[TD([[makeQuery(id+"F12.imprint","IMPRINT",EDGE,{"derivedFrom":sQuery(id+"F12.wireOp",EDGE,"E51.rect.bottom")}),-1.0]])]});
            var Q1;
            {var subQ2=sQuery(id+"F12.wireOp",EDGE,"E55");Q1=makeQuery(id+"F12.imprint","IMPRINT",FACE,{"disambiguationData":[TD([[makeQuery(id+"F12.imprint","IMPRINT",EDGE,{"derivedFrom":subQ2}),-1.0]])]});}
            var Q2;
            {var subQ5=sQuery(id+"F12.wireOp",EDGE,"E60.2.3.0");Q2=makeQuery(id+"F12.imprint","IMPRINT",FACE,{"disambiguationData":[TD([[makeQuery(id+"F12.imprint","IMPRINT",EDGE,{"derivedFrom":subQ5}),-1.0]])]});}
            var Q3;
            {var subQ2=sQuery(id+"F12.wireOp",EDGE,"E59.1.3");Q3=makeQuery(id+"F12.imprint","IMPRINT",FACE,{"disambiguationData":[TD([[makeQuery(id+"F12.imprint","IMPRINT",EDGE,{"derivedFrom":subQ2}),1.0]])]});}
            var Q4;
            {var subQ2=sQuery(id+"F12.wireOp",EDGE,"E59.2.3");Q4=makeQuery(id+"F12.imprint","IMPRINT",FACE,{"disambiguationData":[TD([[makeQuery(id+"F12.imprint","IMPRINT",EDGE,{"derivedFrom":subQ2}),1.0]])]});}
            var Q5;
            {var subQ0=sQuery(id+"F12.wireOp",EDGE,"E79.trimOffspring");Q5=makeQuery(id+"F12.imprint","IMPRINT",FACE,{"disambiguationData":[TD([[makeQuery(id+"F12.imprint","IMPRINT",EDGE,{"derivedFrom":subQ0}),-1.0]])]});}
            var Q6;
            {var subQ3=sQuery(id+"F12.wireOp",EDGE,"E59.1.1");Q6=makeQuery(id+"F12.imprint","IMPRINT",FACE,{"disambiguationData":[TD([[makeQuery(id+"F12.imprint","IMPRINT",EDGE,{"derivedFrom":subQ3}),-1.0]])]});}
            var Q7;
            {var subQ0=sQuery(id+"F12.wireOp",EDGE,"E80.trimOffspring");Q7=makeQuery(id+"F12.imprint","IMPRINT",FACE,{"disambiguationData":[TD([[makeQuery(id+"F12.imprint","IMPRINT",EDGE,{"derivedFrom":subQ0}),-1.0]])]});}
            var Q8;
            {var subQ3=sQuery(id+"F12.wireOp",EDGE,"E59.2.1");Q8=makeQuery(id+"F12.imprint","IMPRINT",FACE,{"disambiguationData":[TD([[makeQuery(id+"F12.imprint","IMPRINT",EDGE,{"derivedFrom":subQ3}),-1.0]])]});}
            var Q9;
            {var subQ9=sQuery(id+"F12.wireOp",EDGE,"E57.rect.top");Q9=makeQuery(id+"F12.imprint","IMPRINT",FACE,{"disambiguationData":[TD([[makeQuery(id+"F12.imprint","IMPRINT",EDGE,{"derivedFrom":subQ9}),1.0]])]});}
            var Q10;
            {var subQ2=sQuery(id+"F12.wireOp",EDGE,"E59.2.1");Q10=makeQuery(id+"F12.imprint","IMPRINT",FACE,{"disambiguationData":[TD([[makeQuery(id+"F12.imprint","IMPRINT",EDGE,{"derivedFrom":subQ2}),1.0]])]});}
            var Q11;
            {var subQ2=sQuery(id+"F12.wireOp",EDGE,"E60.2.3.0");Q11=makeQuery(id+"F12.imprint","IMPRINT",FACE,{"disambiguationData":[TD([[makeQuery(id+"F12.imprint","IMPRINT",EDGE,{"derivedFrom":subQ2}),1.0]])]});}
            var Q12;
            Q12=makeQuery(id+"F12.imprint","IMPRINT",FACE,{"disambiguationData":[TD([[makeQuery(id+"F12.imprint","IMPRINT",EDGE,{"derivedFrom":sQuery(id+"F12.wireOp",EDGE,"E54")}),-1.0]])]});
            var Q13;
            {var subQ2=sQuery(id+"F12.wireOp",EDGE,"E59.1.1");Q13=makeQuery(id+"F12.imprint","IMPRINT",FACE,{"disambiguationData":[TD([[makeQuery(id+"F12.imprint","IMPRINT",EDGE,{"derivedFrom":subQ2}),1.0]])]});}
            extrude(context, id + "F13", {"entities" : qUnion([Q0, Q1, Q2, Q3, Q4, Q5, Q6, Q7, Q8, Q9, Q10, Q11, Q12, Q13]), "depth" : 5 * mm});
        }
        {
            var Q0;
            {var subQ9=sQuery(id+"F12.wireOp",EDGE,"E57.rect.top");Q0=makeQuery(id+"F12.imprint","IMPRINT",FACE,{"disambiguationData":[TD([[makeQuery(id+"F12.imprint","IMPRINT",EDGE,{"derivedFrom":subQ9}),1.0]])]});}
            extrude(context, id + "F14", {"entities" : qUnion([Q0]), "operationType" : NewBodyOperationType.REMOVE, "depth" : 3.5 * mm});
        }
        {
            var Q0;
            Q0=makeQuery(id+"F13.opExtrude","CAP_FACE",FACE,{"disambiguationData":[OSD([sQuery(id+"F12.wireOp",EDGE,"E51.rect.bottom"),sQuery(id+"F12.wireOp",EDGE,"E51.rect.top"),sQuery(id+"F12.wireOp",EDGE,"E51.rect.left"),sQuery(id+"F12.wireOp",EDGE,"E51.rect.right"),sQuery(id+"F12.wireOp",EDGE,"E54"),sQuery(id+"F12.wireOp",EDGE,"E56.filletArc"),sQuery(id+"F12.wireOp",EDGE,"E57.rect.bottom"),sQuery(id+"F12.wireOp",EDGE,"E57.rect.left"),sQuery(id+"F12.wireOp",EDGE,"E59.1.2"),sQuery(id+"F12.wireOp",EDGE,"E59.1.6"),sQuery(id+"F12.wireOp",EDGE,"E59.1.7"),sQuery(id+"F12.wireOp",EDGE,"E59.1.8"),sQuery(id+"F12.wireOp",EDGE,"E59.2.2"),sQuery(id+"F12.wireOp",EDGE,"E59.2.6"),sQuery(id+"F12.wireOp",EDGE,"E59.2.7"),sQuery(id+"F12.wireOp",EDGE,"E59.2.8"),sQuery(id+"F12.wireOp",EDGE,"E60.4.3.0"),sQuery(id+"F12.wireOp",EDGE,"E60.16.3.0"),sQuery(id+"F12.wireOp",EDGE,"E60.19.3.0"),sQuery(id+"F12.wireOp",EDGE,"E60.23.3.0")])],"isStart":false});
            cPlane(context, id + "F15", {"entities" : qUnion([Q0]), "cplaneType" : CPlaneType.OFFSET, "offset" : 0 * mm, "width" : 150 * mm, "height" : 150 * mm});
        }
        {
            var Q0;
            Q0=qCreatedBy(id+"F15.planeOp",FACE);
            var sketch = newSketch(context, id + "F16", { "sketchPlane" : qUnion([Q0])});
            skCircle(sketch, "E92.cCircle", {"center": v(-15.2, 15.2) * mm, "radius": 2.75 * mm, "construction": true});
            skLineSegment(sketch, "E92.0", {"start": v(-16.8, 17.95) * mm, "end": v(-13.62, 17.95) * mm});
            skLineSegment(sketch, "E92.1", {"start": v(-13.62, 17.95) * mm, "end": v(-12.03, 15.2) * mm});
            skLineSegment(sketch, "E92.2", {"start": v(-12.03, 15.2) * mm, "end": v(-13.62, 12.45) * mm});
            skLineSegment(sketch, "E92.3", {"start": v(-13.62, 12.45) * mm, "end": v(-16.8, 12.45) * mm});
            skLineSegment(sketch, "E92.4", {"start": v(-16.8, 12.45) * mm, "end": v(-18.38, 15.2) * mm});
            skLineSegment(sketch, "E92.5", {"start": v(-18.38, 15.2) * mm, "end": v(-16.8, 17.95) * mm});
            skPoint(sketch, "E92.0.midPoint", {"position": v(-15.2, 17.95) * mm});
            skLineSegment(sketch, "E93.MirrorCS", {"start": v(13.62, 17.95) * mm, "end": v(12.03, 15.2) * mm});
            skLineSegment(sketch, "E94.MirrorCS", {"start": v(16.8, 17.95) * mm, "end": v(13.62, 17.95) * mm});
            skLineSegment(sketch, "E95.MirrorCS", {"start": v(18.38, 15.2) * mm, "end": v(16.8, 17.95) * mm});
            skLineSegment(sketch, "E96.MirrorCS", {"start": v(16.8, 12.45) * mm, "end": v(18.38, 15.2) * mm});
            skLineSegment(sketch, "E97.MirrorCS", {"start": v(13.62, 12.45) * mm, "end": v(16.8, 12.45) * mm});
            skLineSegment(sketch, "E98.MirrorCS", {"start": v(12.03, 15.2) * mm, "end": v(13.62, 12.45) * mm});
            skCircle(sketch, "E99.cCircle", {"center": v(-15.2, -15.2) * mm, "radius": 2.75 * mm, "construction": true});
            skLineSegment(sketch, "E99.0", {"start": v(-16.8, -12.45) * mm, "end": v(-13.62, -12.45) * mm});
            skLineSegment(sketch, "E99.1", {"start": v(-13.62, -12.45) * mm, "end": v(-12.03, -15.2) * mm});
            skLineSegment(sketch, "E99.2", {"start": v(-12.03, -15.2) * mm, "end": v(-13.62, -17.95) * mm});
            skLineSegment(sketch, "E99.3", {"start": v(-13.62, -17.95) * mm, "end": v(-16.8, -17.95) * mm});
            skLineSegment(sketch, "E99.4", {"start": v(-16.8, -17.95) * mm, "end": v(-18.38, -15.2) * mm});
            skLineSegment(sketch, "E99.5", {"start": v(-18.38, -15.2) * mm, "end": v(-16.8, -12.45) * mm});
            skPoint(sketch, "E99.0.midPoint", {"position": v(-15.2, -12.45) * mm});
            skLineSegment(sketch, "E100.MirrorCS", {"start": v(16.8, -12.45) * mm, "end": v(13.62, -12.45) * mm});
            skLineSegment(sketch, "E101.MirrorCS", {"start": v(13.62, -12.45) * mm, "end": v(12.03, -15.2) * mm});
            skLineSegment(sketch, "E102.MirrorCS", {"start": v(12.03, -15.2) * mm, "end": v(13.62, -17.95) * mm});
            skLineSegment(sketch, "E103.MirrorCS", {"start": v(13.62, -17.95) * mm, "end": v(16.8, -17.95) * mm});
            skLineSegment(sketch, "E104.MirrorCS", {"start": v(16.8, -17.95) * mm, "end": v(18.38, -15.2) * mm});
            skLineSegment(sketch, "E105.MirrorCS", {"start": v(18.38, -15.2) * mm, "end": v(16.8, -12.45) * mm});
            skSolve(sketch);
        }
        {
            var Q0;
            Q0 = qSketchRegion(id + "F16", true);
            extrude(context, id + "F17", {"entities" : qUnion([Q0]), "operationType" : NewBodyOperationType.REMOVE, "oppositeDirection" : true, "depth" : 2.25 * mm});
        }
        {
            var Q0;
            Q0=qCreatedBy(id+"F11.planeOp",FACE);
            var sketch = newSketch(context, id + "F18", { "sketchPlane" : qUnion([Q0])});
            skLineSegment(sketch, "E106.rect.bottom", {"start": v(4.5, -9.65) * mm, "end": v(-4.5, -9.65) * mm});
            skLineSegment(sketch, "E106.rect.top", {"start": v(4.5, -19.65) * mm, "end": v(-4.5, -19.65) * mm});
            skLineSegment(sketch, "E106.rect.left", {"start": v(4.5, -9.65) * mm, "end": v(4.5, -19.65) * mm});
            skLineSegment(sketch, "E106.rect.right", {"start": v(-4.5, -9.65) * mm, "end": v(-4.5, -19.65) * mm});
            skPoint(sketch, "E106.rect.middle", {"position": v(0, -14.65) * mm});
            skSolve(sketch);
        }
        {
            var Q0;
            Q0 = qSketchRegion(id + "F18", true);
            var Q1;
            Q1=makeQuery(id+"F13.opExtrude","CAP_FACE",FACE,{"disambiguationData":[OSD([sQuery(id+"F12.wireOp",EDGE,"E51.rect.bottom"),sQuery(id+"F12.wireOp",EDGE,"E51.rect.top"),sQuery(id+"F12.wireOp",EDGE,"E51.rect.left"),sQuery(id+"F12.wireOp",EDGE,"E51.rect.right"),sQuery(id+"F12.wireOp",EDGE,"E54"),sQuery(id+"F12.wireOp",EDGE,"E56.filletArc"),sQuery(id+"F12.wireOp",EDGE,"E57.rect.bottom"),sQuery(id+"F12.wireOp",EDGE,"E57.rect.left"),sQuery(id+"F12.wireOp",EDGE,"E59.1.2"),sQuery(id+"F12.wireOp",EDGE,"E59.1.6"),sQuery(id+"F12.wireOp",EDGE,"E59.1.7"),sQuery(id+"F12.wireOp",EDGE,"E59.1.8"),sQuery(id+"F12.wireOp",EDGE,"E59.2.2"),sQuery(id+"F12.wireOp",EDGE,"E59.2.6"),sQuery(id+"F12.wireOp",EDGE,"E59.2.7"),sQuery(id+"F12.wireOp",EDGE,"E59.2.8"),sQuery(id+"F12.wireOp",EDGE,"E60.4.3.0"),sQuery(id+"F12.wireOp",EDGE,"E60.16.3.0"),sQuery(id+"F12.wireOp",EDGE,"E60.19.3.0"),sQuery(id+"F12.wireOp",EDGE,"E60.23.3.0")])],"isStart":false});
            extrude(context, id + "F19", {"entities" : qUnion([Q0]), "operationType" : NewBodyOperationType.REMOVE, "endBound" : BoundingType.UP_TO_SURFACE, "endBoundEntityFace" : qUnion([Q1]), "depth" : 25 * mm});
        }
    });
